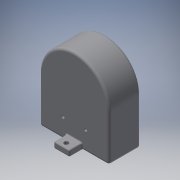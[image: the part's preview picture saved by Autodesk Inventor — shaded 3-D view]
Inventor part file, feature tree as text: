
AUTODESK INVENTOR PART (.ipt)
format: ipt  version: 2018 (Build 220112000, 112)  size: 259,072 bytes
history: native  units: in
note: dims shown in document units (in); Inventor stores cm internally (conversion verified against a paired STEP export)
features: extrude x6, fillet x5, sketch x5, reference x4, plane x1
ambient origin geometry x8: Origin, YZ Plane, XZ Plane, XY Plane, X Axis, Y Axis, Z Axis, Center Point
bodies: Solid1 (feature_tree)
feature tree (21):
  extrude  "Extrusion1"  Depth=0.4in TaperAngle=0.0deg
  extrude  "Extrusion2"  Depth=0.5in
  extrude  "Extrusion4"  Depth=0.4in TaperAngle=0.0deg
  extrude  "Extrusion5"  Depth=0.1378in
  extrude  "Extrusion6"  Depth=0.25in
  plane  "Work Plane1"
  extrude  "Extrusion9"  Depth=0.5in
  fillet  "Fillet1"  Radius=0.197in
  fillet  "Fillet2"  Radius=0.15in
  fillet  "Fillet3"  Radius=0.1772in
  fillet  "Fillet4"  Radius=0.4in
  fillet  "Fillet5"  Radius=0.25in
  sketch  "Sketch1"  dims[d1=1.0in d2=0.0in d4=0.4in d5=0.0in]
  reference  "Reference1"
  sketch  "Sketch2"  dims[d10=0.25in d11=0.5in]
  reference  "Reference2"
  sketch  "Sketch5"  dims[d12=0.197in d13=0.4in d14=0.0in]
  sketch  "Sketch6"  dims[d15=0.15in d16=0.1378in]
  sketch  "Sketch9"  dims[d17=0.4in d18=0.0in d19=0.25in d20=0.5in d21=0.197in d22=0.15in d23=0.1772in d24=0.4in d25=0.0in d26=0.25in d27=2.2in d28=-1.1in d41=0.0394in d42=0.0394in d43=0.098in d44=0.098in d45=1.0in d46=0.0in d47=0.0394in d48=0.0394in d49=0.1575in d50=0.1575in d51=0.0394in]
  reference  "Reference5"
  reference  "Reference6"
